# Revit family: LWPRE
name_source: partatom
category: Lighting Fixtures
units: mm (PartAtom-declared; Revit-internal decimal feet)

## family parameters
Always vertical = Yes
Cut with Voids When Loaded = No
Host = Wall
Light Source = Yes
OmniClass Number = 23.80.70.11.14
OmniClass Title = General Luminaries, Directional
Part Type = Normal
Room Calculation Point = No
Round Connector Dimension = Use Diameter
Shared = No

## types (1)
- LWPRE48-LED840K033LUNV
    Apparent Load = 33 VA
    Assembly Code = D5020200
    Color Filter = 16777215
    Description = LED Wall Prestige
    Dimming Lamp Color Temperature Shift = <None>
    Emit from Line Length = 4' - 2 3/4"
    Housing Finish = Metal - Viscor - White
    Lamp = LED
    Lamp Wattage = 33 VA
    Length = 4' - 2 3/4"
    Lens Finish = Polycarbonate - Viscor -  Soft Matte White Opal
    Manufacturer = VISIONEERING by VISCOR
    Model = LWPRE
    Photometric Web File = LWPRE48-LED840K033LUNV.ies
    Tilt Angle = 180.00°
    URL = https://www.viscor.com
    Voltage = 120 V

## geometry (parser evidence)
native form markers: Sweep x3
no freeform markers — native parametric forms only
